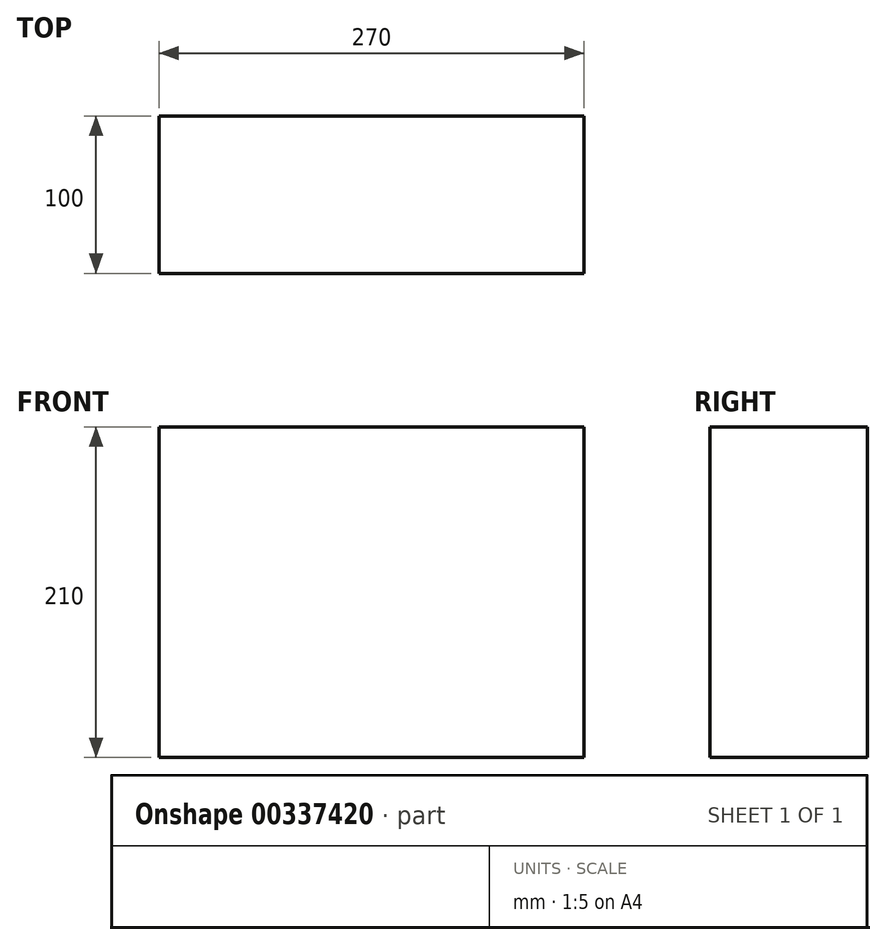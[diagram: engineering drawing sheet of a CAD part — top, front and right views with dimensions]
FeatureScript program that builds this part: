
annotation { "Feature Type Name" : "Feature", "Feature Type Description" : "" }
export const myFeature = defineFeature(function(context is Context, id is Id, definition is map)
    precondition{}
    {
        {
            var Q0;
            Q0=qCreatedBy(makeId("Front.planeOp"),FACE);
            var sketch = newSketch(context, id + "F0", { "sketchPlane" : qUnion([Q0])});
            skLineSegment(sketch, "E0.bottom", {"start": v(-135, 105) * mm, "end": v(135, 105) * mm});
            skLineSegment(sketch, "E0.top", {"start": v(-135, -105) * mm, "end": v(135, -105) * mm});
            skLineSegment(sketch, "E0.left", {"start": v(-135, 105) * mm, "end": v(-135, -105) * mm});
            skLineSegment(sketch, "E0.right", {"start": v(135, 105) * mm, "end": v(135, -105) * mm});
            skLineSegment(sketch, "E1", {"start": v(-135, -105) * mm, "end": v(135, 105) * mm, "construction": true});
            skSolve(sketch);
        }
        {
            var Q0;
            Q0=qSketchRegion(id+"F0",true);
            extrude(context, id + "F1", {"entities" : qUnion([Q0]), "depth" : 100 * mm});
        }
    });
